# Revit family: IVLB_L4U_LF_Forsite 865 PE
name_source: partatom
category: Lighting Fixtures
units: mm (PartAtom-declared; Revit-internal decimal feet)

## family parameters
Always vertical = Yes
Cut with Voids When Loaded = No
Light Source = Yes
OmniClass Number = 23.80.70.11.14.11
OmniClass Title = Downlights
Part Type = Normal
Room Calculation Point = Yes
Round Connector Dimension = Use Diameter
Shared = No
Work Plane-Based = No

## types (8) — shared parameters
Assembly Code = 63.0
Calc_L1_Symbol = 9 mm  [stored 0.0295276 ft]
Calc_L2_Symbol = 1 mm  [stored 0.00328084 ft]
Color Filter = 16777215
Dimming Lamp Color Temperature Shift = <None>
ETIM Code = -
Emit Shape Visible in Rendering = No
Emit from Rectangle Length = 851 mm  [stored 2.79199 ft]
Emit from Rectangle Width = 52 mm  [stored 0.170604 ft]
GTIN Code = -
H1 = 55 mm  [stored 0.180446 ft]
Housing_Material = Select RGB Value for different appearance
IK Value = -
IP Value = IP20
ISBN Code = -
IfcExportAs = IfcLightFixtureType
IfcExportType = USERDEFINED
L1 = 865 mm  [stored 2.83793 ft]
L2 = 66 mm  [stored 0.216535 ft]
L3 = 7 mm  [stored 0.0229659 ft]
L4 = 800 mm  [stored 2.62467 ft]
LED Panel = Yes
Lamp = LED
Manufacturer = Light4U
Model = Forsite
Tilt Angle = 90.00°
Type Comments = 865 PE
URL = www.light4u.com
Voltage = 230 V

## per-type parameters (varying)
| type | Apparent Load | Luminous Flux (lm) | Photometric Web File | Wattage Comments |
| Forsite 865 6950lm_830 52W 90deg | 51 VA | 6950 lm | Forsite 865 6950lm_830 52W 90deg.ies | 51 |
| Forsite 865 7300lm_840 52W 90deg | 51 VA | 7300 lm | Forsite 865 7300lm_840 52W 90deg.ies | 51 |
| Forsite 865 7150lm_840 52W DA | 52 VA | 7150 lm | Forsite 865 7150lm_840 52W DA.ies | 52 |
| Forsite 865 6800lm_830 52W DA | 52 VA | 6800 lm | Forsite 865 6800lm_830 52W DA.ies | 52 |
| Forsite 865 6680lm_840 52W 30deg | 51 VA | 6680 lm | Forsite 865 6680lm_840 52W 30deg.ies | 51 |
| Forsite 865 6600lm_840 52W 60deg | 51 VA | 6600 lm | Forsite 865 6600lm_840 52W 60deg.ies | 51 |
| Forsite 865 6350lm_830 52W 30deg | 51 VA | 6369 lm | Forsite 865 6350lm_830 52W 30deg.ies | 51 |
| Forsite 865 6300lm 830 52W 60deg | 51 VA | 6300 lm | Forsite 865 6300lm 830 52W 60deg.ies | 51 |

note: [stored X ft] marks values corroborated as IEEE doubles in the binary element streams (Revit-internal decimal feet)

## geometry (parser evidence)
native form markers: Sweep x7
no freeform markers — native parametric forms only
